# Revit family: 4069994 Sylvania Lighting Fixture PATHE CEILING ROUND5 MEDIUM 1251LM LED 3K
name_source: partatom
category: Lighting Fixtures
revit_build: Autodesk Revit 2016 (Build: 20150220_1215(x64)
units: mm (PartAtom-declared; Revit-internal decimal feet)

## family parameters
Cut with Voids When Loaded = No
Host = Face
Light Source = No
OmniClass Number = 23.80.70.00
OmniClass Title = Lighting
Part Type = Normal
Room Calculation Point = No
Round Connector Dimension = Use Diameter
Shared = No

## types (1)
- 4069994 PATHE/C/R5 MED 1251LM LED 3K
    Apparent Load = 22 VA
    Assembly Code = D5020200
    AssetType = Fixed
    ChamferDiffuserSide_SYL = 2 mm  [stored 0.00656168 ft]
    ChamferDiffuserTop_SYL = 10 mm  [stored 0.0328084 ft]
    ChamferTop_SYL = 4 mm  [stored 0.0131234 ft]
    ClassificationName = Uniclass2015
    ClassificationValue = EF_70_80
    Cost = 0 $
    Default Elevation = 1219 mm
    Description = Round recessed ceiling mounted luminaireCorrosion resistant anodized aluminium, 1251lm, 22,4W, 56lm/W, 3000K, CRI80+, medium, non dimmable, IP66, IK10, (ØxD) 290x210mm, 3 step MacAdam ellipse, 6.7kg, Class I, 220-240V, A++ A+ A
    DocumentationLiterature = http://www.sylvania-lighting.com
    DurationUnit = hours
    ElectricShockClassification = Class I
    ExpectedLife = 50000
    HieghtTop_SYL = 4 mm  [stored 0.0131234 ft]
    IfcExportAs = IfcLightFixtureType
    IfcExportType = IfcLightFixtureType
    ImpactProtectionIndex = IK10
    IngressProtection = IP66
    Keynote = 16500
    Lamp = LED
    LampColourRenderingIndex = 80
    LampColourTemperature = 3000 K
    LampNominalLuminous = 1251 lm
    LampsType = LED
    LightOutputRatio = 100
    LuminousEfficacy = 55.84 lm/W
    Manufacturer = Feilo Sylvania
    ManufacturerName = Feilo Sylvania
    Material = corrosion resistant die-cast aluminium body. aluminium fixing bracket. housing, tempered safety glass - 12 mm thickness, mechanical and thermal shock resistant diffuser
    Material_1_SYL = Aluminum 6061 T6 80 Hot Formed
    Material_2_SYL = LED-Sylvania
    Material_3_SYL = Inside_Sylvania_Pathe_Black
    Material_4_SYL = Polycarbonate, Clear
    Material_5_SYL = Steel AISI 1006 85 HR
    Model = PATHE/CEILING/ROUND5 MEDIUM 1251LM LED 3K
    ModelNumber = 4069994
    ModelReference = PATHE/CEILING/ROUND5 MEDIUM 1251LM LED 3K
    Name = PATHE/CEILING/ROUND5 MEDIUM 1251LM LED 3K
    NominalDepth = 0 mm  [stored 0 ft]
    NominalHeight = 0 mm  [stored 0 ft]
    NominalLength = 315 mm  [stored 1.03346 ft]
    PowerConsumption = 22.4 W
    PowerFactor = 0
    RadiusDiffuser_SYL = 116 mm
    RadiusS_SYL = 88 mm
    Radius_SYL = 158 mm
    Type Image = <None>
    TypeHead_SYL = Pathe Round 5 Lamp : 4069994 PATHE/C/R5 MED 1251LM LED 3K
    TypeName = PATHE/CEILING/ROUND5 MEDIUM 1251LM LED 3K
    URL = http://www.sylvania-lighting.com
    Voltage = 0 V
    Weight = 6.4 kg

note: [stored X ft] marks values corroborated as IEEE doubles in the binary element streams (Revit-internal decimal feet)

## geometry (parser evidence)
native form markers: Revolve x2, Sweep x8
no freeform markers — native parametric forms only
